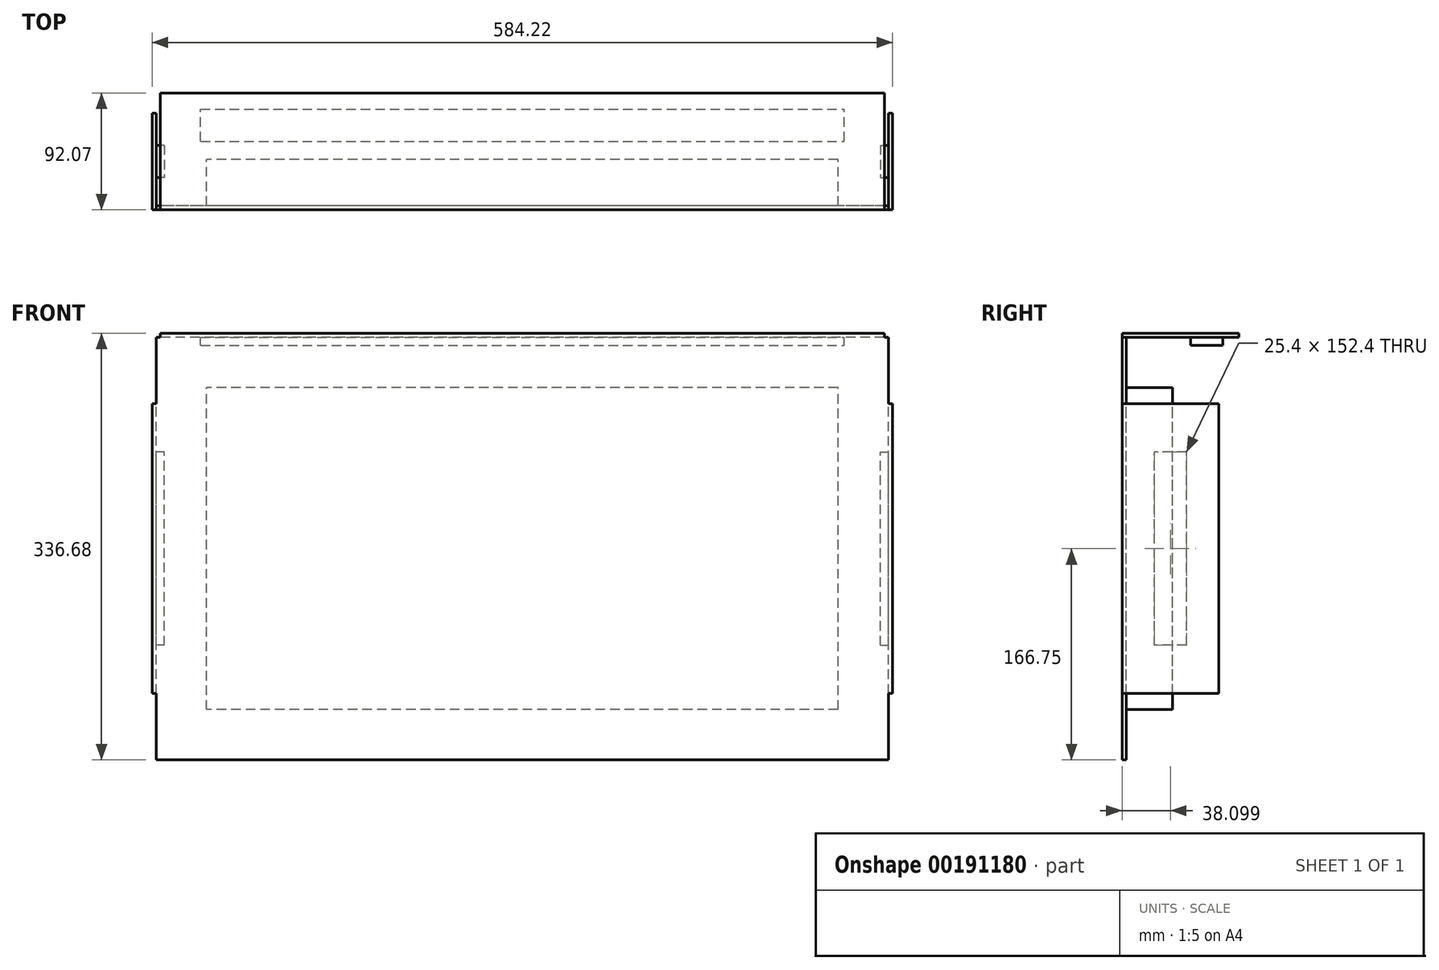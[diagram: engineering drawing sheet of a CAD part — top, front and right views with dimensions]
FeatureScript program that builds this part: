
annotation { "Feature Type Name" : "Feature", "Feature Type Description" : "" }
export const myFeature = defineFeature(function(context is Context, id is Id, definition is map)
    precondition{}
    {
        {
            var Q0;
            Q0=qCreatedBy(makeId("Front.planeOp"),FACE);
            var sketch = newSketch(context, id + "F0", { "sketchPlane" : qUnion([Q0])});
            skLineSegment(sketch, "E0.bottom", {"start": v(249.24, -127) * mm, "end": v(-249.24, -127) * mm});
            skLineSegment(sketch, "E0.top", {"start": v(249.24, 127) * mm, "end": v(-249.24, 127) * mm});
            skLineSegment(sketch, "E0.left", {"start": v(249.24, -127) * mm, "end": v(249.24, 127) * mm});
            skLineSegment(sketch, "E0.right", {"start": v(-249.24, -127) * mm, "end": v(-249.24, 127) * mm});
            skPoint(sketch, "E0.middle", {"position": v(0, 0) * mm});
            skSolve(sketch);
        }
        {
            var Q0;
            Q0=qSketchRegion(id+"F0",true);
            extrude(context, id + "F1", {"entities" : qUnion([Q0]), "depth" : 36.58 * mm});
        }
        {
            var Q0;
            Q0=makeQuery(id+"F1.opExtrude","CAP_FACE",FACE,{"disambiguationData":[OSD([sQuery(id+"F0.wireOp",EDGE,"E0.bottom"),sQuery(id+"F0.wireOp",EDGE,"E0.top"),sQuery(id+"F0.wireOp",EDGE,"E0.left"),sQuery(id+"F0.wireOp",EDGE,"E0.right")])],"isStart":false});
            var sketch = newSketch(context, id + "F2", { "sketchPlane" : qUnion([Q0])});
            skLineSegment(sketch, "E1.bottom", {"start": v(288.94, -166.75) * mm, "end": v(-288.94, -166.75) * mm});
            skLineSegment(sketch, "E1.top", {"start": v(288.94, 166.75) * mm, "end": v(-288.94, 166.75) * mm});
            skLineSegment(sketch, "E1.left", {"start": v(288.94, -166.75) * mm, "end": v(288.94, 166.75) * mm});
            skLineSegment(sketch, "E1.right", {"start": v(-288.94, -166.75) * mm, "end": v(-288.94, 166.75) * mm});
            skPoint(sketch, "E1.middle", {"position": v(0, 0) * mm});
            skSolve(sketch);
        }
        {
            var Q0;
            Q0 = qSketchRegion(id + "F2", true);
            extrude(context, id + "F3", {"entities" : qUnion([Q0]), "operationType" : NewBodyOperationType.ADD, "depth" : 3.17 * mm});
        }
        {
            var Q0;
            Q0=makeQuery(id+"F3.opExtrude","SWEPT_FACE",FACE,{"disambiguationData":[OSD([sQuery(id+"F2.wireOp",EDGE,"E1.left")])]});
            var sketch = newSketch(context, id + "F4", { "sketchPlane" : qUnion([Q0])});
            skLineSegment(sketch, "E2.bottom", {"start": v(-39.75, 114.3) * mm, "end": v(36.45, 114.3) * mm});
            skLineSegment(sketch, "E2.top", {"start": v(-39.75, -114.3) * mm, "end": v(36.45, -114.3) * mm});
            skLineSegment(sketch, "E2.left", {"start": v(-39.75, 114.3) * mm, "end": v(-39.75, -114.3) * mm});
            skLineSegment(sketch, "E2.right", {"start": v(36.45, 114.3) * mm, "end": v(36.45, -114.3) * mm});
            skPoint(sketch, "E3", {"position": v(-1.65, 0) * mm});
            skLineSegment(sketch, "E4", {"start": v(-51.71, 0) * mm, "end": v(63.15, 0) * mm});
            skSolve(sketch);
        }
        {
            var Q0;
            Q0 = qSketchRegion(id + "F4", true);
            extrude(context, id + "F5", {"entities" : qUnion([Q0]), "operationType" : NewBodyOperationType.ADD, "depth" : 3.17 * mm});
        }
        {
            var Q0;
            Q0=makeQuery(id+"F3.opExtrude","SWEPT_FACE",FACE,{"disambiguationData":[OSD([sQuery(id+"F2.wireOp",EDGE,"E1.right")])]});
            var sketch = newSketch(context, id + "F6", { "sketchPlane" : qUnion([Q0])});
            skLineSegment(sketch, "E5.bottom", {"start": v(39.75, 114.3) * mm, "end": v(-36.45, 114.3) * mm});
            skLineSegment(sketch, "E5.top", {"start": v(39.75, -114.3) * mm, "end": v(-36.45, -114.3) * mm});
            skLineSegment(sketch, "E5.left", {"start": v(39.75, 114.3) * mm, "end": v(39.75, -114.3) * mm});
            skLineSegment(sketch, "E5.right", {"start": v(-36.45, 114.3) * mm, "end": v(-36.45, -114.3) * mm});
            skPoint(sketch, "E6", {"position": v(1.65, 0) * mm});
            skSolve(sketch);
        }
        {
            var Q0;
            Q0 = qSketchRegion(id + "F6", true);
            extrude(context, id + "F7", {"entities" : qUnion([Q0]), "operationType" : NewBodyOperationType.ADD, "depth" : 3.17 * mm});
        }
        {
            var Q0;
            Q0=makeQuery(id+"F7.opExtrude","CAP_FACE",FACE,{"disambiguationData":[OSD([sQuery(id+"F6.wireOp",EDGE,"E5.bottom"),sQuery(id+"F6.wireOp",EDGE,"E5.top"),sQuery(id+"F6.wireOp",EDGE,"E5.left"),sQuery(id+"F6.wireOp",EDGE,"E5.right")])],"isStart":true});
            var sketch = newSketch(context, id + "F8", { "sketchPlane" : qUnion([Q0])});
            skLineSegment(sketch, "E7.bottom", {"start": v(11.05, -76.2) * mm, "end": v(-14.35, -76.2) * mm});
            skLineSegment(sketch, "E7.top", {"start": v(11.05, 76.2) * mm, "end": v(-14.35, 76.2) * mm});
            skLineSegment(sketch, "E7.left", {"start": v(11.05, -76.2) * mm, "end": v(11.05, 76.2) * mm});
            skLineSegment(sketch, "E7.right", {"start": v(-14.35, -76.2) * mm, "end": v(-14.35, 76.2) * mm});
            skPoint(sketch, "E7.middle", {"position": v(-1.65, 0) * mm});
            skSolve(sketch);
        }
        {
            var Q0;
            Q0 = qSketchRegion(id + "F8", true);
            extrude(context, id + "F9", {"entities" : qUnion([Q0]), "operationType" : NewBodyOperationType.ADD, "depth" : 6.35 * mm});
        }
        {
            var Q0;
            Q0=makeQuery(id+"F5.opExtrude","CAP_FACE",FACE,{"disambiguationData":[OSD([sQuery(id+"F4.wireOp",EDGE,"E2.bottom"),sQuery(id+"F4.wireOp",EDGE,"E2.top"),sQuery(id+"F4.wireOp",EDGE,"E2.left"),sQuery(id+"F4.wireOp",EDGE,"E2.right")])],"isStart":true});
            var sketch = newSketch(context, id + "F10", { "sketchPlane" : qUnion([Q0])});
            skLineSegment(sketch, "E8.bottom", {"start": v(-11.05, -76.2) * mm, "end": v(14.35, -76.2) * mm});
            skLineSegment(sketch, "E8.top", {"start": v(-11.05, 76.2) * mm, "end": v(14.35, 76.2) * mm});
            skLineSegment(sketch, "E8.left", {"start": v(-11.05, -76.2) * mm, "end": v(-11.05, 76.2) * mm});
            skLineSegment(sketch, "E8.right", {"start": v(14.35, -76.2) * mm, "end": v(14.35, 76.2) * mm});
            skPoint(sketch, "E8.middle", {"position": v(1.65, 0) * mm});
            skSolve(sketch);
        }
        {
            var Q0;
            Q0 = qSketchRegion(id + "F10", true);
            extrude(context, id + "F11", {"entities" : qUnion([Q0]), "operationType" : NewBodyOperationType.ADD, "depth" : 6.35 * mm});
        }
        {
            var Q0;
            Q0=makeQuery(id+"F3.opExtrude","SWEPT_FACE",FACE,{"disambiguationData":[OSD([sQuery(id+"F2.wireOp",EDGE,"E1.top")])]});
            var sketch = newSketch(context, id + "F12", { "sketchPlane" : qUnion([Q0])});
            skLineSegment(sketch, "E9.bottom", {"start": v(-285.75, 52.32) * mm, "end": v(285.75, 52.32) * mm});
            skLineSegment(sketch, "E9.top", {"start": v(-285.75, -39.75) * mm, "end": v(285.75, -39.75) * mm});
            skLineSegment(sketch, "E9.left", {"start": v(-285.75, 52.32) * mm, "end": v(-285.75, -39.75) * mm});
            skLineSegment(sketch, "E9.right", {"start": v(285.75, 52.32) * mm, "end": v(285.75, -39.75) * mm});
            skPoint(sketch, "E9.middle", {"position": v(0, 6.29) * mm});
            skSolve(sketch);
        }
        {
            var Q0;
            Q0 = qSketchRegion(id + "F12", true);
            extrude(context, id + "F13", {"entities" : qUnion([Q0]), "operationType" : NewBodyOperationType.ADD, "depth" : 3.17 * mm});
        }
        {
            var Q0;
            Q0=makeQuery(id+"F13.opExtrude","CAP_FACE",FACE,{"disambiguationData":[OSD([sQuery(id+"F12.wireOp",EDGE,"E9.bottom"),sQuery(id+"F12.wireOp",EDGE,"E9.top"),sQuery(id+"F12.wireOp",EDGE,"E9.left"),sQuery(id+"F12.wireOp",EDGE,"E9.right")])],"isStart":true});
            var sketch = newSketch(context, id + "F14", { "sketchPlane" : qUnion([Q0])});
            skLineSegment(sketch, "E10.bottom", {"start": v(-254, -14.22) * mm, "end": v(254, -14.22) * mm});
            skLineSegment(sketch, "E10.top", {"start": v(-254, -39.62) * mm, "end": v(254, -39.62) * mm});
            skLineSegment(sketch, "E10.left", {"start": v(-254, -14.22) * mm, "end": v(-254, -39.62) * mm});
            skLineSegment(sketch, "E10.right", {"start": v(254, -14.22) * mm, "end": v(254, -39.62) * mm});
            skPoint(sketch, "E10.middle", {"position": v(0, -26.92) * mm});
            skSolve(sketch);
        }
        {
            var Q0;
            Q0 = qSketchRegion(id + "F14", true);
            extrude(context, id + "F15", {"entities" : qUnion([Q0]), "operationType" : NewBodyOperationType.ADD, "depth" : 6.35 * mm});
        }
    });
